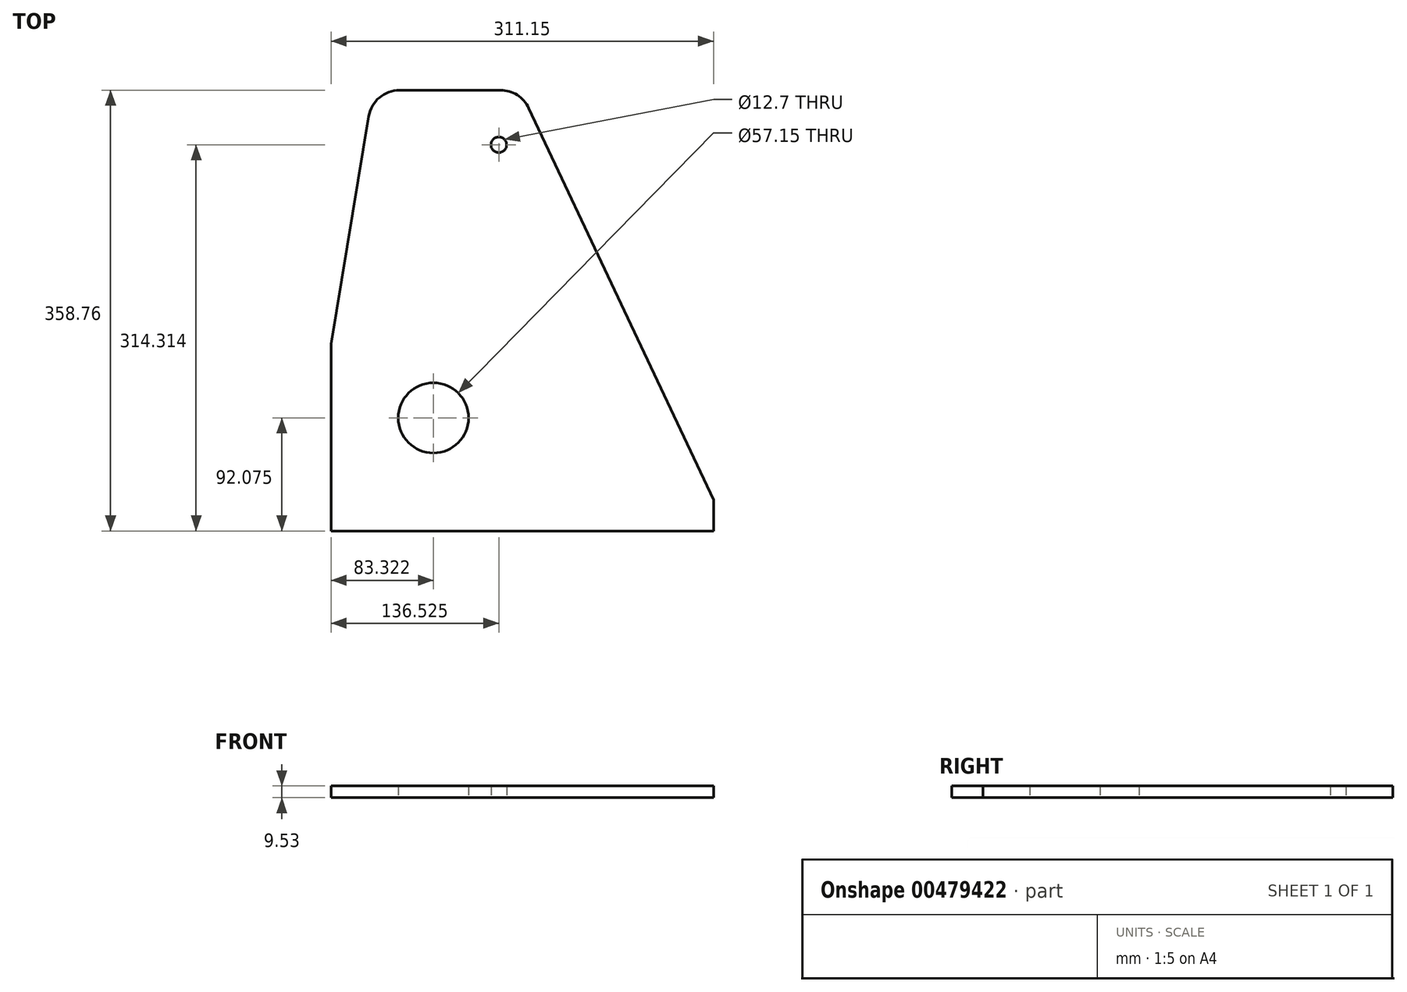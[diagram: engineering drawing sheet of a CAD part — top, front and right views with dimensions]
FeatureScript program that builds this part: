
annotation { "Feature Type Name" : "Feature", "Feature Type Description" : "" }
export const myFeature = defineFeature(function(context is Context, id is Id, definition is map)
    precondition{}
    {
        {
            var Q0;
            Q0=qCreatedBy(makeId("Top.planeOp"),FACE);
            var sketch = newSketch(context, id + "F0", { "sketchPlane" : qUnion([Q0]), "disableImprinting" : false});
            skLineSegment(sketch, "E0", {"start": v(0, 0) * mm, "end": v(0, 152.4) * mm});
            skLineSegment(sketch, "E1", {"start": v(0, 152.4) * mm, "end": v(30.72, 337.52) * mm});
            skLineSegment(sketch, "E2", {"start": v(0, 0) * mm, "end": v(311.15, 0) * mm});
            skLineSegment(sketch, "E3", {"start": v(311.15, 0) * mm, "end": v(311.15, 25.4) * mm});
            skLineSegment(sketch, "E4", {"start": v(311.15, 25.4) * mm, "end": v(160.9, 344.2) * mm});
            skCircle(sketch, "E5", {"center": v(55.78, 333.36) * mm, "radius": 25.4 * mm});
            skCircle(sketch, "E6", {"center": v(137.93, 333.36) * mm, "radius": 25.4 * mm});
            skLineSegment(sketch, "E7", {"start": v(55.78, 358.76) * mm, "end": v(137.93, 358.76) * mm});
            skCircle(sketch, "E8", {"center": v(111.62, 262.57) * mm, "radius": 28.58 * mm});
            skCircle(sketch, "E9", {"center": v(83.32, 92.07) * mm, "radius": 28.58 * mm});
            skCircle(sketch, "E10", {"center": v(191.98, 92.08) * mm, "radius": 28.58 * mm});
            skLineSegment(sketch, "E11", {"start": v(83.32, 63.5) * mm, "end": v(191.98, 63.5) * mm});
            skLineSegment(sketch, "E12", {"start": v(137.47, 274.76) * mm, "end": v(217.82, 104.26) * mm});
            skLineSegment(sketch, "E13", {"start": v(83.45, 267.38) * mm, "end": v(55.15, 96.86) * mm});
            skCircle(sketch, "E14", {"center": v(136.53, 314.31) * mm, "radius": 6.35 * mm});
            skSolve(sketch);
        }
        {
            var Q0;
            Q0 = qSketchRegion(id + "F0", true);
            extrude(context, id + "F1", {"entities" : qUnion([Q0]), "depth" : 9.52 * mm, "offsetDistance" : 25.4 * mm});
        }
    });
